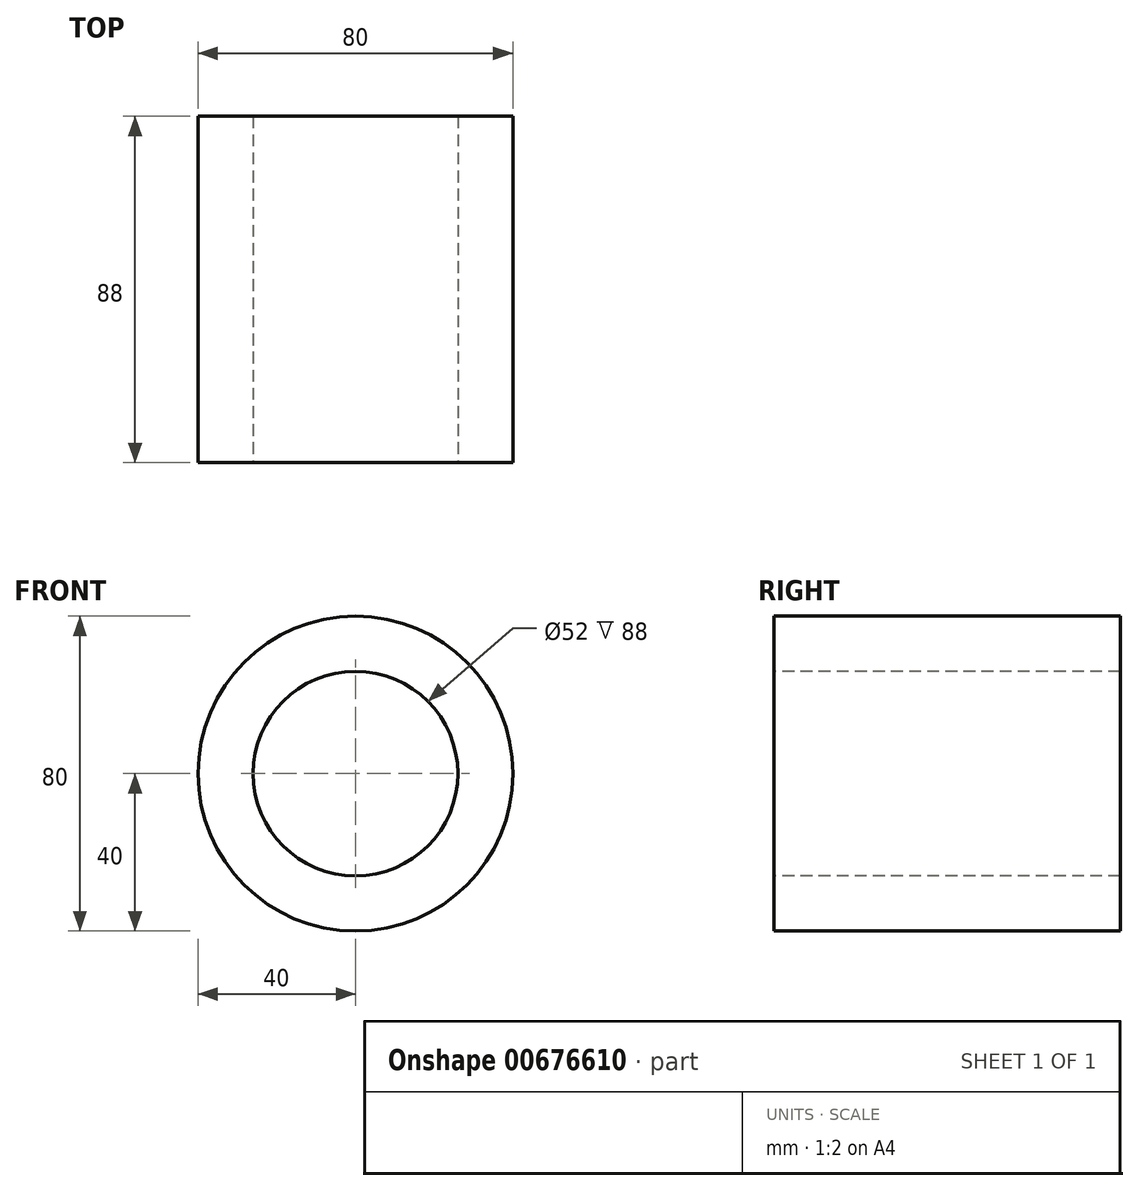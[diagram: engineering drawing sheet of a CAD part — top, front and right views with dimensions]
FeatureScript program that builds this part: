
annotation { "Feature Type Name" : "Feature", "Feature Type Description" : "" }
export const myFeature = defineFeature(function(context is Context, id is Id, definition is map)
    precondition{}
    {
        {
            var Q0;
            Q0=qCreatedBy(makeId("Front.planeOp"),FACE);
            var sketch = newSketch(context, id + "F0", { "sketchPlane" : qUnion([Q0])});
            skCircle(sketch, "E0", {"center": v(0, 0) * mm, "radius": 22 * mm});
            skCircle(sketch, "E1", {"center": v(0, 0) * mm, "radius": 6 * mm});
            skCircle(sketch, "E2", {"center": v(0, 0) * mm, "radius": 26 * mm});
            skCircle(sketch, "E3", {"center": v(0, 0) * mm, "radius": 40 * mm});
            skSolve(sketch);
        }
        {
            var Q0;
            Q0=makeQuery(id+"F0.imprint","IMPRINT",FACE,{"disambiguationData":[TD([[makeQuery(id+"F0.imprint","IMPRINT",EDGE,{"derivedFrom":sQuery(id+"F0.wireOp",EDGE,"E2")}),-1.0]])]});
            extrude(context, id + "F1", {"entities" : qUnion([Q0]), "oppositeDirection" : true, "depth" : 88 * mm, "offsetDistance" : 25 * mm});
        }
    });
